# Revit family: Papelera Mielek
name_source: partatom
category: Furniture
units: mm (PartAtom-declared; Revit-internal decimal feet)

## family parameters
Always vertical = Yes
Cut with Voids When Loaded = No
OmniClass Number = 23.40.20.00
OmniClass Title = General Furniture and Specialties
Room Calculation Point = No
Shared = No
Work Plane-Based = No

## types (4) — shared parameters
A = 410 mm  [stored 1.34514 ft]
B = 410 mm  [stored 1.34514 ft]
Description = Papelera fabricada en acero con tratamiento Ferrus, proceso protector del hierro, que garantiza una óptima resistencia a la corrosión.
Fabricante = BENITO URBAN SL
Ficha Tecnica = https://www.benito.com
H = 920 mm  [stored 3.01837 ft]
Material = Acero Ferrus
Type Comments = Anclaje recomendado: Mediante cuatro pernos de expansión de Ø10 según superficie y proyecto
URL Producto = https://www.benito.com
zero-valued in all types: Default Elevation

## per-type parameters (varying)
| type | Color | Referencia |
| Papelera Mielek S-PA691SV-410mm | Mielek SV | PA691SV |
| Papelera Mielek SR-PA691SR-410mm | Mielek SR | PA691SR |
| Papelera Mielek SO-PA691SO-410mm | Mielek SO | PA691SO |
| Papelera Mielek M-PA691M-410mm | Mielek M | PA691M |

note: [stored X ft] marks values corroborated as IEEE doubles in the binary element streams (Revit-internal decimal feet)

## geometry (parser evidence)
native form markers: Blend x2, Sweep x3
no freeform markers — native parametric forms only
